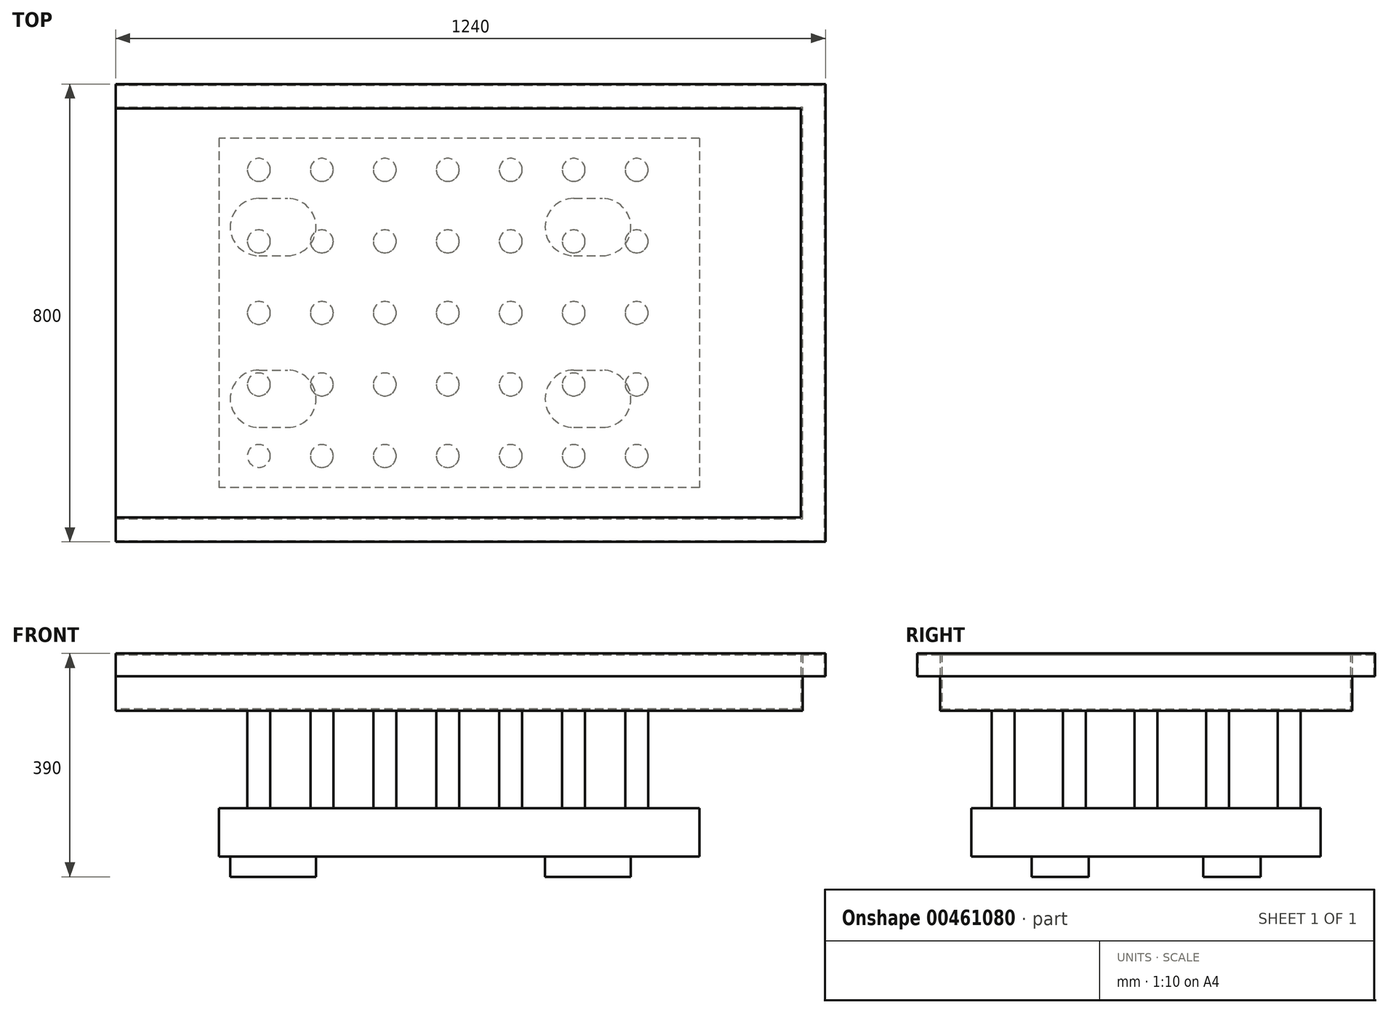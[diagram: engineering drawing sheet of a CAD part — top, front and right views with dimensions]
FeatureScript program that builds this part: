
annotation { "Feature Type Name" : "Feature", "Feature Type Description" : "" }
export const myFeature = defineFeature(function(context is Context, id is Id, definition is map)
    precondition{}
    {
        {
            var Q0;
            Q0=qCreatedBy(makeId("Top.planeOp"),FACE);
            var sketch = newSketch(context, id + "F0", { "sketchPlane" : qUnion([Q0])});
            skLineSegment(sketch, "E0.bottom", {"start": v(600, -360) * mm, "end": v(-600, -360) * mm});
            skLineSegment(sketch, "E0.top", {"start": v(600, 360) * mm, "end": v(-600, 360) * mm});
            skLineSegment(sketch, "E0.left", {"start": v(600, -360) * mm, "end": v(600, 360) * mm});
            skLineSegment(sketch, "E0.right", {"start": v(-600, -360) * mm, "end": v(-600, 360) * mm});
            skPoint(sketch, "E0.middle", {"position": v(0, 0) * mm});
            skSolve(sketch);
        }
        {
            var Q0;
            Q0 = qSketchRegion(id + "F0", true);
            extrude(context, id + "F1", {"entities" : qUnion([Q0]), "depth" : 100 * mm});
        }
        {
            var Q0;
            Q0=makeQuery(id+"F1.opExtrude","CAP_FACE",FACE,{"disambiguationData":[OSD([sQuery(id+"F0.wireOp",EDGE,"E0.bottom"),sQuery(id+"F0.wireOp",EDGE,"E0.top"),sQuery(id+"F0.wireOp",EDGE,"E0.left"),sQuery(id+"F0.wireOp",EDGE,"E0.right")])],"isStart":false});
            shell(context, id + "F2", {"entities" : qUnion([Q0]), "thickness" : 3 * mm});
        }
        {
            var Q0;
            Q0=makeQuery(id+"F2.opShell","OFFSET_FACE",FACE,{"disambiguationData":[OSD([sQuery(id+"F0.wireOp",EDGE,"E0.right")])]});
            extrude(context, id + "F3", {"entities" : qUnion([Q0]), "operationType" : NewBodyOperationType.REMOVE, "endBound" : BoundingType.UP_TO_NEXT, "oppositeDirection" : true, "depth" : 25 * mm});
        }
        {
            var Q0;
            Q0=makeQuery(id+"F1.opExtrude","CAP_FACE",FACE,{"disambiguationData":[OSD([sQuery(id+"F0.wireOp",EDGE,"E0.bottom"),sQuery(id+"F0.wireOp",EDGE,"E0.top"),sQuery(id+"F0.wireOp",EDGE,"E0.left"),sQuery(id+"F0.wireOp",EDGE,"E0.right")])],"isStart":true});
            var sketch = newSketch(context, id + "F4", { "sketchPlane" : qUnion([Q0])});
            skCircle(sketch, "E1", {"center": v(-350, 250) * mm, "radius": 20 * mm});
            skCircle(sketch, "E2.0.1.0", {"center": v(-350, 125) * mm, "radius": 20 * mm});
            skCircle(sketch, "E2.0.2.0", {"center": v(-350, 0) * mm, "radius": 20 * mm});
            skCircle(sketch, "E2.0.3.0", {"center": v(-350, -125) * mm, "radius": 20 * mm});
            skCircle(sketch, "E2.1.0.0", {"center": v(-240, 250) * mm, "radius": 20 * mm});
            skCircle(sketch, "E2.1.1.0", {"center": v(-240, 125) * mm, "radius": 20 * mm});
            skCircle(sketch, "E2.1.2.0", {"center": v(-240, 0) * mm, "radius": 20 * mm});
            skCircle(sketch, "E2.1.3.0", {"center": v(-240, -125) * mm, "radius": 20 * mm});
            skCircle(sketch, "E2.2.0.0", {"center": v(-130, 250) * mm, "radius": 20 * mm});
            skCircle(sketch, "E2.2.1.0", {"center": v(-130, 125) * mm, "radius": 20 * mm});
            skCircle(sketch, "E2.2.2.0", {"center": v(-130, 0) * mm, "radius": 20 * mm});
            skCircle(sketch, "E2.2.3.0", {"center": v(-130, -125) * mm, "radius": 20 * mm});
            skCircle(sketch, "E2.3.0.0", {"center": v(-20, 250) * mm, "radius": 20 * mm});
            skCircle(sketch, "E2.3.1.0", {"center": v(-20, 125) * mm, "radius": 20 * mm});
            skCircle(sketch, "E2.3.2.0", {"center": v(-20, 0) * mm, "radius": 20 * mm});
            skCircle(sketch, "E2.3.3.0", {"center": v(-20, -125) * mm, "radius": 20 * mm});
            skCircle(sketch, "E2.4.0.0", {"center": v(90, 250) * mm, "radius": 20 * mm});
            skCircle(sketch, "E2.4.1.0", {"center": v(90, 125) * mm, "radius": 20 * mm});
            skCircle(sketch, "E2.4.2.0", {"center": v(90, 0) * mm, "radius": 20 * mm});
            skCircle(sketch, "E2.4.3.0", {"center": v(90, -125) * mm, "radius": 20 * mm});
            skCircle(sketch, "E2.5.0.0", {"center": v(200, 250) * mm, "radius": 20 * mm});
            skCircle(sketch, "E2.5.1.0", {"center": v(200, 125) * mm, "radius": 20 * mm});
            skCircle(sketch, "E2.5.2.0", {"center": v(200, 0) * mm, "radius": 20 * mm});
            skCircle(sketch, "E2.5.3.0", {"center": v(200, -125) * mm, "radius": 20 * mm});
            skCircle(sketch, "E2.6.0.0", {"center": v(310, 250) * mm, "radius": 20 * mm});
            skCircle(sketch, "E2.6.1.0", {"center": v(310, 125) * mm, "radius": 20 * mm});
            skCircle(sketch, "E2.6.2.0", {"center": v(310, 0) * mm, "radius": 20 * mm});
            skCircle(sketch, "E2.6.3.0", {"center": v(310, -125) * mm, "radius": 20 * mm});
            skLineSegment(sketch, "E2.direction1", {"start": v(-350, 250) * mm, "end": v(-240, 250) * mm, "construction": true});
            skLineSegment(sketch, "E2.direction2", {"start": v(-350, 250) * mm, "end": v(-350, 125) * mm, "construction": true});
            skCircle(sketch, "E3.0.0.4", {"center": v(-350, -250) * mm, "radius": 20 * mm});
            skCircle(sketch, "E3.0.1.4", {"center": v(-240, -250) * mm, "radius": 20 * mm});
            skCircle(sketch, "E3.0.2.4", {"center": v(-130, -250) * mm, "radius": 20 * mm});
            skCircle(sketch, "E3.0.3.4", {"center": v(-20, -250) * mm, "radius": 20 * mm});
            skCircle(sketch, "E3.0.4.4", {"center": v(90, -250) * mm, "radius": 20 * mm});
            skCircle(sketch, "E3.0.5.4", {"center": v(200, -250) * mm, "radius": 20 * mm});
            skCircle(sketch, "E3.0.6.4", {"center": v(310, -250) * mm, "radius": 20 * mm});
            skSolve(sketch);
        }
        {
            var Q0;
            Q0 = qSketchRegion(id + "F4", true);
            extrude(context, id + "F5", {"entities" : qUnion([Q0]), "operationType" : NewBodyOperationType.ADD, "depth" : 170 * mm});
        }
        {
            var Q0;
            Q0=makeQuery(id+"F5.opExtrude","CAP_FACE",FACE,{"disambiguationData":[OSD([sQuery(id+"F4.wireOp",EDGE,"E2.4.2.0")])],"isStart":false});
            var sketch = newSketch(context, id + "F6", { "sketchPlane" : qUnion([Q0])});
            skLineSegment(sketch, "E4.bottom", {"start": v(420, -305) * mm, "end": v(-420, -305) * mm});
            skLineSegment(sketch, "E4.top", {"start": v(420, 305) * mm, "end": v(-420, 305) * mm});
            skLineSegment(sketch, "E4.left", {"start": v(420, -305) * mm, "end": v(420, 305) * mm});
            skLineSegment(sketch, "E4.right", {"start": v(-420, -305) * mm, "end": v(-420, 305) * mm});
            skPoint(sketch, "E4.middle", {"position": v(0, 0) * mm});
            skSolve(sketch);
        }
        {
            var Q0;
            Q0 = qSketchRegion(id + "F6", true);
            extrude(context, id + "F7", {"entities" : qUnion([Q0]), "operationType" : NewBodyOperationType.ADD, "depth" : 85 * mm});
        }
        {
            var Q0;
            Q0=makeQuery(id+"F7.opExtrude","CAP_FACE",FACE,{"disambiguationData":[OSD([sQuery(id+"F6.wireOp",EDGE,"E4.bottom"),sQuery(id+"F6.wireOp",EDGE,"E4.top"),sQuery(id+"F6.wireOp",EDGE,"E4.left"),sQuery(id+"F6.wireOp",EDGE,"E4.right")])],"isStart":false});
            var sketch = newSketch(context, id + "F8", { "sketchPlane" : qUnion([Q0])});
            skLineSegment(sketch, "E5", {"start": v(-350, 200) * mm, "end": v(-300, 200) * mm});
            skLineSegment(sketch, "E6", {"start": v(-350, 100) * mm, "end": v(-300, 100) * mm});
            skArc(sketch, "E7", {"start": v(-300, 200) * mm, "mid": v(-250, 150) * mm, "end": v(-300, 100) * mm});
            skArc(sketch, "E8", {"start": v(-350, 200) * mm, "mid": v(-400, 150) * mm, "end": v(-350, 100) * mm});
            skLineSegment(sketch, "E9", {"start": v(200, 200) * mm, "end": v(250, 200) * mm});
            skLineSegment(sketch, "E10", {"start": v(200, 100) * mm, "end": v(250, 100) * mm});
            skArc(sketch, "E11", {"start": v(250, 200) * mm, "mid": v(300, 150) * mm, "end": v(250, 100) * mm});
            skArc(sketch, "E12", {"start": v(200, 200) * mm, "mid": v(150, 150) * mm, "end": v(200, 100) * mm});
            skLineSegment(sketch, "E13", {"start": v(-350, -100) * mm, "end": v(-300, -100) * mm});
            skLineSegment(sketch, "E14", {"start": v(-350, -200) * mm, "end": v(-300, -200) * mm});
            skArc(sketch, "E15", {"start": v(-300, -100) * mm, "mid": v(-250, -150) * mm, "end": v(-300, -200) * mm});
            skArc(sketch, "E16", {"start": v(-350, -100) * mm, "mid": v(-400, -150) * mm, "end": v(-350, -200) * mm});
            skLineSegment(sketch, "E17", {"start": v(200, -100) * mm, "end": v(250, -100) * mm});
            skLineSegment(sketch, "E18", {"start": v(200, -200) * mm, "end": v(250, -200) * mm});
            skArc(sketch, "E19", {"start": v(250, -100) * mm, "mid": v(300, -150) * mm, "end": v(250, -200) * mm});
            skArc(sketch, "E20", {"start": v(200, -100) * mm, "mid": v(150, -150) * mm, "end": v(200, -200) * mm});
            skSolve(sketch);
        }
        {
            var Q0;
            Q0 = qSketchRegion(id + "F8", true);
            extrude(context, id + "F9", {"entities" : qUnion([Q0]), "operationType" : NewBodyOperationType.ADD, "depth" : 35 * mm});
        }
        {
            var Q0;
            Q0=makeQuery(id+"F1.opExtrude","SWEPT_FACE",FACE,{"disambiguationData":[OSD([sQuery(id+"F0.wireOp",EDGE,"E0.left")])]});
            var sketch = newSketch(context, id + "F10", { "sketchPlane" : qUnion([Q0])});
            skLineSegment(sketch, "E21", {"start": v(-360, 100) * mm, "end": v(-400, 100) * mm});
            skLineSegment(sketch, "E22", {"start": v(-400, 100) * mm, "end": v(-400, 60) * mm});
            skLineSegment(sketch, "E23", {"start": v(360, 100) * mm, "end": v(400, 100) * mm});
            skLineSegment(sketch, "E24", {"start": v(400, 100) * mm, "end": v(400, 60) * mm});
            skLineSegment(sketch, "E25", {"start": v(-400, 60) * mm, "end": v(-398, 60) * mm});
            skLineSegment(sketch, "E26", {"start": v(-398, 60) * mm, "end": v(-398, 98) * mm});
            skLineSegment(sketch, "E27", {"start": v(-398, 98) * mm, "end": v(-360, 98) * mm});
            skLineSegment(sketch, "E28", {"start": v(-360, 98) * mm, "end": v(-360, 100) * mm});
            skLineSegment(sketch, "E29", {"start": v(400, 60) * mm, "end": v(398, 60) * mm});
            skLineSegment(sketch, "E30", {"start": v(398, 60) * mm, "end": v(398, 98) * mm});
            skLineSegment(sketch, "E31", {"start": v(398, 98) * mm, "end": v(360, 98) * mm});
            skLineSegment(sketch, "E32", {"start": v(360, 98) * mm, "end": v(360, 100) * mm});
            skSolve(sketch);
        }
        {
            var Q0;
            Q0=makeQuery(id+"F10.imprint","IMPRINT",FACE,{"disambiguationData":[TD([[makeQuery(id+"F10.imprint","IMPRINT",EDGE,{"derivedFrom":sQuery(id+"F10.wireOp",EDGE,"E23")}),-1.0]])]});
            var Q1;
            Q1=makeQuery(id+"F10.imprint","IMPRINT",FACE,{"disambiguationData":[TD([[makeQuery(id+"F10.imprint","IMPRINT",EDGE,{"derivedFrom":sQuery(id+"F10.wireOp",EDGE,"E21")}),1.0]])]});
            extrude(context, id + "F11", {"entities" : qUnion([Q0, Q1]), "operationType" : NewBodyOperationType.ADD, "oppositeDirection" : true, "depth" : 1200 * mm});
        }
        {
            var Q0;
            Q0=makeQuery(id+"F11.boolean.opBoolean","MERGE",FACE,{"derivedFrom":[makeQuery(id+"F1.opExtrude","CAP_FACE",FACE,{"disambiguationData":[OSD([sQuery(id+"F0.wireOp",EDGE,"E0.bottom"),sQuery(id+"F0.wireOp",EDGE,"E0.top"),sQuery(id+"F0.wireOp",EDGE,"E0.left"),sQuery(id+"F0.wireOp",EDGE,"E0.right")])],"isStart":false}),makeQuery(id+"F11.opExtrude","SWEPT_FACE",FACE,{"disambiguationData":[OSD([sQuery(id+"F10.wireOp",EDGE,"E21")])]}),makeQuery(id+"F11.opExtrude","SWEPT_FACE",FACE,{"disambiguationData":[OSD([sQuery(id+"F10.wireOp",EDGE,"E23")])]})]});
            var sketch = newSketch(context, id + "F12", { "sketchPlane" : qUnion([Q0])});
            skLineSegment(sketch, "E33", {"start": v(600, 400) * mm, "end": v(640, 400) * mm});
            skLineSegment(sketch, "E34", {"start": v(640, 400) * mm, "end": v(640, -400) * mm});
            skLineSegment(sketch, "E35", {"start": v(640, -400) * mm, "end": v(600, -400) * mm});
            skLineSegment(sketch, "E36", {"start": v(600, -400) * mm, "end": v(600, 400) * mm});
            skSolve(sketch);
        }
        {
            var Q0;
            Q0=makeQuery(id+"F12.imprint","IMPRINT",FACE,{"disambiguationData":[TD([[makeQuery(id+"F12.imprint","IMPRINT",EDGE,{"derivedFrom":sQuery(id+"F12.wireOp",EDGE,"E33")}),-1.0]])]});
            extrude(context, id + "F13", {"entities" : qUnion([Q0]), "operationType" : NewBodyOperationType.ADD, "oppositeDirection" : true, "depth" : 2 * mm});
        }
        {
            var Q0;
            Q0=makeQuery(id+"F13.boolean.opBoolean","MERGE",FACE,{"derivedFrom":[makeQuery(id+"F11.opExtrude","SWEPT_FACE",FACE,{"disambiguationData":[OSD([sQuery(id+"F10.wireOp",EDGE,"E27")])]}),makeQuery(id+"F11.opExtrude","SWEPT_FACE",FACE,{"disambiguationData":[OSD([sQuery(id+"F10.wireOp",EDGE,"E31")])]}),makeQuery(id+"F13.opExtrude","CAP_FACE",FACE,{"disambiguationData":[OSD([sQuery(id+"F12.wireOp",EDGE,"E33"),sQuery(id+"F12.wireOp",EDGE,"E34"),sQuery(id+"F12.wireOp",EDGE,"E35"),sQuery(id+"F12.wireOp",EDGE,"E36")])],"isStart":false})]});
            var sketch = newSketch(context, id + "F14", { "sketchPlane" : qUnion([Q0])});
            skLineSegment(sketch, "E37", {"start": v(600, -398) * mm, "end": v(600, -400) * mm});
            skLineSegment(sketch, "E38", {"start": v(600, -400) * mm, "end": v(640, -400) * mm});
            skLineSegment(sketch, "E39", {"start": v(640, -400) * mm, "end": v(640, 400) * mm});
            skLineSegment(sketch, "E40", {"start": v(640, 400) * mm, "end": v(600, 400) * mm});
            skLineSegment(sketch, "E41", {"start": v(600, 400) * mm, "end": v(600, 398) * mm});
            skLineSegment(sketch, "E42", {"start": v(600, 398) * mm, "end": v(638, 398) * mm});
            skLineSegment(sketch, "E43", {"start": v(638, 398) * mm, "end": v(638, -398) * mm});
            skLineSegment(sketch, "E44", {"start": v(638, -398) * mm, "end": v(600, -398) * mm});
            skSolve(sketch);
        }
        {
            var Q0;
            Q0=makeQuery(id+"F14.imprint","IMPRINT",FACE,{"disambiguationData":[TD([[makeQuery(id+"F14.imprint","IMPRINT",EDGE,{"derivedFrom":sQuery(id+"F14.wireOp",EDGE,"E37")}),1.0]])]});
            extrude(context, id + "F15", {"entities" : qUnion([Q0]), "operationType" : NewBodyOperationType.ADD, "depth" : 38 * mm});
        }
    });
